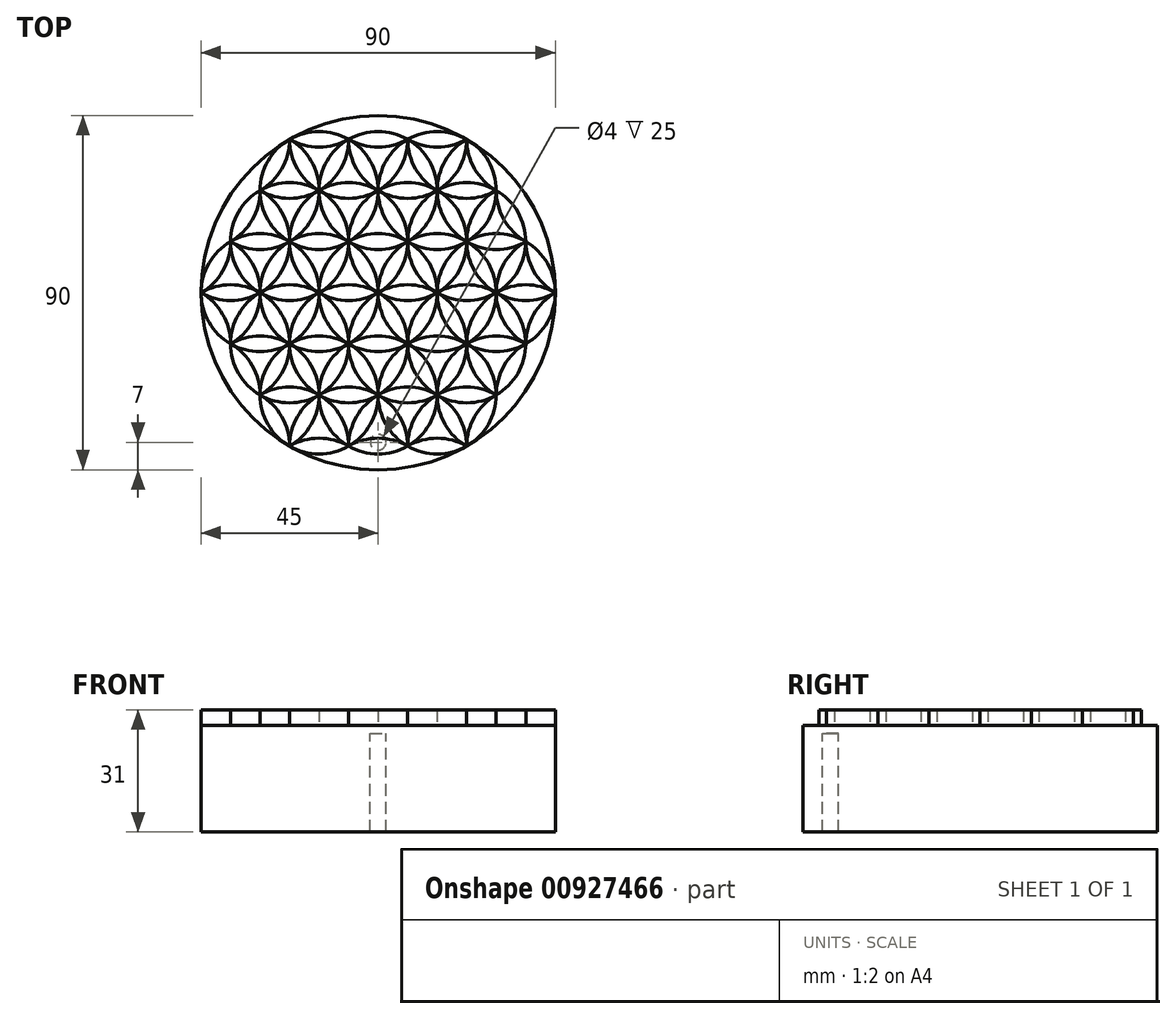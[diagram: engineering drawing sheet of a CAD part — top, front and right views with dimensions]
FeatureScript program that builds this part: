
annotation { "Feature Type Name" : "Feature", "Feature Type Description" : "" }
export const myFeature = defineFeature(function(context is Context, id is Id, definition is map)
    precondition{}
    {
        {
            var Q0;
            Q0=qCreatedBy(makeId("Top.planeOp"),FACE);
            var sketch = newSketch(context, id + "F0", { "sketchPlane" : qUnion([Q0])});
            skCircle(sketch, "E0", {"center": v(0, 0) * mm, "radius": 15 * mm});
            skCircle(sketch, "E1", {"center": v(15, 0) * mm, "radius": 15 * mm});
            skCircle(sketch, "E2", {"center": v(7.5, -13) * mm, "radius": 15 * mm});
            skCircle(sketch, "E3", {"center": v(-7.5, -13) * mm, "radius": 15 * mm});
            skCircle(sketch, "E4", {"center": v(-15, 0) * mm, "radius": 15 * mm});
            skCircle(sketch, "E5", {"center": v(-7.5, 13) * mm, "radius": 15 * mm});
            skCircle(sketch, "E6", {"center": v(7.5, 13) * mm, "radius": 15 * mm});
            skCircle(sketch, "E7", {"center": v(22.5, 13) * mm, "radius": 15 * mm});
            skCircle(sketch, "E8", {"center": v(-22.5, 13) * mm, "radius": 15 * mm});
            skCircle(sketch, "E9", {"center": v(-22.5, -13) * mm, "radius": 15 * mm});
            skCircle(sketch, "E10", {"center": v(-15, 25.98) * mm, "radius": 15 * mm});
            skCircle(sketch, "E11", {"center": v(0, 25.98) * mm, "radius": 15 * mm});
            skCircle(sketch, "E12", {"center": v(15, 25.98) * mm, "radius": 15 * mm});
            skCircle(sketch, "E13", {"center": v(7.5, 38.97) * mm, "radius": 15 * mm});
            skCircle(sketch, "E14", {"center": v(-7.5, 38.97) * mm, "radius": 15 * mm});
            skCircle(sketch, "E15", {"center": v(22.5, -13) * mm, "radius": 15 * mm});
            skCircle(sketch, "E16", {"center": v(30, 0) * mm, "radius": 15 * mm});
            skCircle(sketch, "E17", {"center": v(-30, 0) * mm, "radius": 15 * mm});
            skCircle(sketch, "E18", {"center": v(-15, -25.98) * mm, "radius": 15 * mm});
            skCircle(sketch, "E19", {"center": v(0, -25.98) * mm, "radius": 15 * mm});
            skCircle(sketch, "E20", {"center": v(15, -25.98) * mm, "radius": 15 * mm});
            skCircle(sketch, "E21", {"center": v(7.5, -38.97) * mm, "radius": 15 * mm});
            skCircle(sketch, "E22", {"center": v(-7.5, -38.97) * mm, "radius": 15 * mm});
            skCircle(sketch, "E23", {"center": v(30, -25.98) * mm, "radius": 15 * mm});
            skCircle(sketch, "E24", {"center": v(37.5, -13) * mm, "radius": 15 * mm});
            skCircle(sketch, "E25", {"center": v(-30, -25.98) * mm, "radius": 15 * mm});
            skCircle(sketch, "E26", {"center": v(-37.5, -13) * mm, "radius": 15 * mm});
            skCircle(sketch, "E27", {"center": v(-22.5, -38.97) * mm, "radius": 15 * mm});
            skCircle(sketch, "E28", {"center": v(22.5, -38.97) * mm, "radius": 15 * mm});
            skCircle(sketch, "E29", {"center": v(30, 25.98) * mm, "radius": 15 * mm});
            skCircle(sketch, "E30", {"center": v(37.5, 13) * mm, "radius": 15 * mm});
            skCircle(sketch, "E31", {"center": v(-30, 25.98) * mm, "radius": 15 * mm});
            skCircle(sketch, "E32", {"center": v(-37.5, 13) * mm, "radius": 15 * mm});
            skCircle(sketch, "E33", {"center": v(45, 0) * mm, "radius": 15 * mm});
            skCircle(sketch, "E34", {"center": v(45, -25.98) * mm, "radius": 15 * mm});
            skCircle(sketch, "E35", {"center": v(0, -51.96) * mm, "radius": 15 * mm});
            skCircle(sketch, "E36", {"center": v(0, 51.96) * mm, "radius": 15 * mm});
            skCircle(sketch, "E37", {"center": v(22.5, 38.97) * mm, "radius": 15 * mm});
            skCircle(sketch, "E38", {"center": v(-22.5, 38.97) * mm, "radius": 15 * mm});
            skCircle(sketch, "E39", {"center": v(-45, 0) * mm, "radius": 15 * mm});
            skCircle(sketch, "E40", {"center": v(-15, -51.96) * mm, "radius": 15 * mm});
            skCircle(sketch, "E41", {"center": v(15, -51.96) * mm, "radius": 15 * mm});
            skCircle(sketch, "E42", {"center": v(-45, -25.98) * mm, "radius": 15 * mm});
            skCircle(sketch, "E43", {"center": v(-37.5, -38.97) * mm, "radius": 15 * mm});
            skCircle(sketch, "E44", {"center": v(-52.5, 13) * mm, "radius": 15 * mm});
            skCircle(sketch, "E45", {"center": v(-45, 25.98) * mm, "radius": 15 * mm});
            skCircle(sketch, "E46", {"center": v(-37.5, 38.97) * mm, "radius": 15 * mm});
            skCircle(sketch, "E47", {"center": v(37.5, -38.97) * mm, "radius": 15 * mm});
            skCircle(sketch, "E48", {"center": v(-15, 51.96) * mm, "radius": 15 * mm});
            skCircle(sketch, "E49", {"center": v(-52.5, -13) * mm, "radius": 15 * mm});
            skCircle(sketch, "E50", {"center": v(15, 51.96) * mm, "radius": 15 * mm});
            skCircle(sketch, "E51", {"center": v(52.5, -13) * mm, "radius": 15 * mm});
            skCircle(sketch, "E52", {"center": v(37.5, 38.97) * mm, "radius": 15 * mm});
            skCircle(sketch, "E53", {"center": v(45, 25.98) * mm, "radius": 15 * mm});
            skCircle(sketch, "E54", {"center": v(52.5, 13) * mm, "radius": 15 * mm});
            skSolve(sketch);
        }
        {
            var Q0;
            {var subQ0=sQuery(id+"F0.wireOp",EDGE,"E6");var subQ1=sQuery(id+"F0.wireOp",EDGE,"E2");var subQ2=makeQuery(id+"F0.imprint","INTERSECT",VERTEX,{"derivedFrom":[sQuery(id+"F0.wireOp",EDGE,"E0"),subQ1,subQ0,sQuery(id+"F0.wireOp",EDGE,"E7"),sQuery(id+"F0.wireOp",EDGE,"E15"),sQuery(id+"F0.wireOp",EDGE,"E16")]});Q0=makeQuery(id+"F0.imprint","IMPRINT",FACE,{"disambiguationData":[TD([[makeQuery(id+"F0.imprint","IMPRINT",EDGE,{"disambiguationData":[TD([[subQ2,-1.0]])],"derivedFrom":subQ1}),1.0]])]});}
            var Q1;
            {var subQ0=sQuery(id+"F0.wireOp",EDGE,"E5");var subQ1=sQuery(id+"F0.wireOp",EDGE,"E1");var subQ2=makeQuery(id+"F0.imprint","INTERSECT",VERTEX,{"derivedFrom":[sQuery(id+"F0.wireOp",EDGE,"E0"),subQ1,subQ0,sQuery(id+"F0.wireOp",EDGE,"E7"),sQuery(id+"F0.wireOp",EDGE,"E11"),sQuery(id+"F0.wireOp",EDGE,"E12")]});Q1=makeQuery(id+"F0.imprint","IMPRINT",FACE,{"disambiguationData":[TD([[makeQuery(id+"F0.imprint","IMPRINT",EDGE,{"disambiguationData":[TD([[subQ2,-1.0]])],"derivedFrom":subQ1}),1.0]])]});}
            var Q2;
            {var subQ0=sQuery(id+"F0.wireOp",EDGE,"E6");var subQ1=sQuery(id+"F0.wireOp",EDGE,"E4");var subQ2=makeQuery(id+"F0.imprint","INTERSECT",VERTEX,{"derivedFrom":[sQuery(id+"F0.wireOp",EDGE,"E0"),subQ1,subQ0,sQuery(id+"F0.wireOp",EDGE,"E8"),sQuery(id+"F0.wireOp",EDGE,"E10"),sQuery(id+"F0.wireOp",EDGE,"E11")]});Q2=makeQuery(id+"F0.imprint","IMPRINT",FACE,{"disambiguationData":[TD([[makeQuery(id+"F0.imprint","IMPRINT",EDGE,{"disambiguationData":[TD([[subQ2,1.0]])],"derivedFrom":subQ1}),1.0]])]});}
            var Q3;
            {var subQ0=sQuery(id+"F0.wireOp",EDGE,"E5");var subQ1=sQuery(id+"F0.wireOp",EDGE,"E3");var subQ2=makeQuery(id+"F0.imprint","INTERSECT",VERTEX,{"derivedFrom":[sQuery(id+"F0.wireOp",EDGE,"E0"),subQ1,subQ0,sQuery(id+"F0.wireOp",EDGE,"E8"),sQuery(id+"F0.wireOp",EDGE,"E9"),sQuery(id+"F0.wireOp",EDGE,"E17")]});Q3=makeQuery(id+"F0.imprint","IMPRINT",FACE,{"disambiguationData":[TD([[makeQuery(id+"F0.imprint","IMPRINT",EDGE,{"disambiguationData":[TD([[subQ2,1.0]])],"derivedFrom":subQ1}),1.0]])]});}
            var Q4;
            {var subQ0=sQuery(id+"F0.wireOp",EDGE,"E4");var subQ1=sQuery(id+"F0.wireOp",EDGE,"E2");var subQ2=makeQuery(id+"F0.imprint","INTERSECT",VERTEX,{"derivedFrom":[sQuery(id+"F0.wireOp",EDGE,"E0"),subQ1,subQ0,sQuery(id+"F0.wireOp",EDGE,"E9"),sQuery(id+"F0.wireOp",EDGE,"E18"),sQuery(id+"F0.wireOp",EDGE,"E19")]});Q4=makeQuery(id+"F0.imprint","IMPRINT",FACE,{"disambiguationData":[TD([[makeQuery(id+"F0.imprint","IMPRINT",EDGE,{"disambiguationData":[TD([[subQ2,1.0]])],"derivedFrom":subQ1}),1.0]])]});}
            var Q5;
            {var subQ0=sQuery(id+"F0.wireOp",EDGE,"E3");var subQ1=sQuery(id+"F0.wireOp",EDGE,"E1");var subQ2=makeQuery(id+"F0.imprint","INTERSECT",VERTEX,{"derivedFrom":[sQuery(id+"F0.wireOp",EDGE,"E0"),subQ1,subQ0,sQuery(id+"F0.wireOp",EDGE,"E15"),sQuery(id+"F0.wireOp",EDGE,"E19"),sQuery(id+"F0.wireOp",EDGE,"E20")]});Q5=makeQuery(id+"F0.imprint","IMPRINT",FACE,{"disambiguationData":[TD([[makeQuery(id+"F0.imprint","IMPRINT",EDGE,{"disambiguationData":[TD([[subQ2,1.0]])],"derivedFrom":subQ1}),1.0]])]});}
            var Q6;
            {var subQ0=sQuery(id+"F0.wireOp",EDGE,"E15");var subQ1=sQuery(id+"F0.wireOp",EDGE,"E0");var subQ2=makeQuery(id+"F0.imprint","INTERSECT",VERTEX,{"derivedFrom":[subQ1,sQuery(id+"F0.wireOp",EDGE,"E2"),sQuery(id+"F0.wireOp",EDGE,"E6"),sQuery(id+"F0.wireOp",EDGE,"E7"),subQ0,sQuery(id+"F0.wireOp",EDGE,"E16")]});Q6=makeQuery(id+"F0.imprint","IMPRINT",FACE,{"disambiguationData":[TD([[makeQuery(id+"F0.imprint","IMPRINT",EDGE,{"disambiguationData":[TD([[subQ2,1.0]])],"derivedFrom":subQ1}),1.0]])]});}
            var Q7;
            {var subQ0=sQuery(id+"F0.wireOp",EDGE,"E7");var subQ1=sQuery(id+"F0.wireOp",EDGE,"E0");var subQ2=makeQuery(id+"F0.imprint","INTERSECT",VERTEX,{"derivedFrom":[subQ1,sQuery(id+"F0.wireOp",EDGE,"E1"),sQuery(id+"F0.wireOp",EDGE,"E5"),subQ0,sQuery(id+"F0.wireOp",EDGE,"E11"),sQuery(id+"F0.wireOp",EDGE,"E12")]});Q7=makeQuery(id+"F0.imprint","IMPRINT",FACE,{"disambiguationData":[TD([[makeQuery(id+"F0.imprint","IMPRINT",EDGE,{"disambiguationData":[TD([[subQ2,1.0]])],"derivedFrom":subQ1}),1.0]])]});}
            var Q8;
            {var subQ0=sQuery(id+"F0.wireOp",EDGE,"E11");var subQ1=sQuery(id+"F0.wireOp",EDGE,"E0");var subQ2=makeQuery(id+"F0.imprint","INTERSECT",VERTEX,{"derivedFrom":[subQ1,sQuery(id+"F0.wireOp",EDGE,"E1"),sQuery(id+"F0.wireOp",EDGE,"E5"),sQuery(id+"F0.wireOp",EDGE,"E7"),subQ0,sQuery(id+"F0.wireOp",EDGE,"E12")]});Q8=makeQuery(id+"F0.imprint","IMPRINT",FACE,{"disambiguationData":[TD([[makeQuery(id+"F0.imprint","IMPRINT",EDGE,{"disambiguationData":[TD([[subQ2,-1.0]])],"derivedFrom":subQ1}),1.0]])]});}
            var Q9;
            {var subQ0=sQuery(id+"F0.wireOp",EDGE,"E8");var subQ1=sQuery(id+"F0.wireOp",EDGE,"E0");var subQ2=makeQuery(id+"F0.imprint","INTERSECT",VERTEX,{"derivedFrom":[subQ1,sQuery(id+"F0.wireOp",EDGE,"E4"),sQuery(id+"F0.wireOp",EDGE,"E6"),subQ0,sQuery(id+"F0.wireOp",EDGE,"E10"),sQuery(id+"F0.wireOp",EDGE,"E11")]});Q9=makeQuery(id+"F0.imprint","IMPRINT",FACE,{"disambiguationData":[TD([[makeQuery(id+"F0.imprint","IMPRINT",EDGE,{"disambiguationData":[TD([[subQ2,-1.0]])],"derivedFrom":subQ1}),1.0]])]});}
            var Q10;
            {var subQ0=sQuery(id+"F0.wireOp",EDGE,"E9");var subQ1=sQuery(id+"F0.wireOp",EDGE,"E0");var subQ2=makeQuery(id+"F0.imprint","INTERSECT",VERTEX,{"derivedFrom":[subQ1,sQuery(id+"F0.wireOp",EDGE,"E3"),sQuery(id+"F0.wireOp",EDGE,"E5"),sQuery(id+"F0.wireOp",EDGE,"E8"),subQ0,sQuery(id+"F0.wireOp",EDGE,"E17")]});Q10=makeQuery(id+"F0.imprint","IMPRINT",FACE,{"disambiguationData":[TD([[makeQuery(id+"F0.imprint","IMPRINT",EDGE,{"disambiguationData":[TD([[subQ2,-1.0]])],"derivedFrom":subQ1}),1.0]])]});}
            var Q11;
            {var subQ0=sQuery(id+"F0.wireOp",EDGE,"E19");var subQ1=sQuery(id+"F0.wireOp",EDGE,"E0");var subQ2=makeQuery(id+"F0.imprint","INTERSECT",VERTEX,{"derivedFrom":[subQ1,sQuery(id+"F0.wireOp",EDGE,"E2"),sQuery(id+"F0.wireOp",EDGE,"E4"),sQuery(id+"F0.wireOp",EDGE,"E9"),sQuery(id+"F0.wireOp",EDGE,"E18"),subQ0]});Q11=makeQuery(id+"F0.imprint","IMPRINT",FACE,{"disambiguationData":[TD([[makeQuery(id+"F0.imprint","IMPRINT",EDGE,{"disambiguationData":[TD([[subQ2,-1.0]])],"derivedFrom":subQ1}),1.0]])]});}
            var Q12;
            {var subQ0=sQuery(id+"F0.wireOp",EDGE,"E18");var subQ1=sQuery(id+"F0.wireOp",EDGE,"E4");var subQ2=makeQuery(id+"F0.imprint","INTERSECT",VERTEX,{"derivedFrom":[sQuery(id+"F0.wireOp",EDGE,"E0"),sQuery(id+"F0.wireOp",EDGE,"E2"),subQ1,sQuery(id+"F0.wireOp",EDGE,"E9"),subQ0,sQuery(id+"F0.wireOp",EDGE,"E19")]});Q12=makeQuery(id+"F0.imprint","IMPRINT",FACE,{"disambiguationData":[TD([[makeQuery(id+"F0.imprint","IMPRINT",EDGE,{"disambiguationData":[TD([[subQ2,1.0]])],"derivedFrom":subQ1}),1.0]])]});}
            var Q13;
            {var subQ0=sQuery(id+"F0.wireOp",EDGE,"E19");var subQ1=sQuery(id+"F0.wireOp",EDGE,"E9");var subQ2=makeQuery(id+"F0.imprint","INTERSECT",VERTEX,{"derivedFrom":[sQuery(id+"F0.wireOp",EDGE,"E0"),sQuery(id+"F0.wireOp",EDGE,"E2"),sQuery(id+"F0.wireOp",EDGE,"E4"),subQ1,sQuery(id+"F0.wireOp",EDGE,"E18"),subQ0]});Q13=makeQuery(id+"F0.imprint","IMPRINT",FACE,{"disambiguationData":[TD([[makeQuery(id+"F0.imprint","IMPRINT",EDGE,{"disambiguationData":[TD([[subQ2,1.0]])],"derivedFrom":subQ1}),1.0]])]});}
            var Q14;
            {var subQ0=sQuery(id+"F0.wireOp",EDGE,"E18");var subQ1=sQuery(id+"F0.wireOp",EDGE,"E2");var subQ2=makeQuery(id+"F0.imprint","INTERSECT",VERTEX,{"derivedFrom":[sQuery(id+"F0.wireOp",EDGE,"E0"),subQ1,sQuery(id+"F0.wireOp",EDGE,"E4"),sQuery(id+"F0.wireOp",EDGE,"E9"),subQ0,sQuery(id+"F0.wireOp",EDGE,"E19")]});Q14=makeQuery(id+"F0.imprint","IMPRINT",FACE,{"disambiguationData":[TD([[makeQuery(id+"F0.imprint","IMPRINT",EDGE,{"disambiguationData":[TD([[subQ2,-1.0]])],"derivedFrom":subQ1}),1.0]])]});}
            var Q15;
            {var subQ0=sQuery(id+"F0.wireOp",EDGE,"E20");var subQ1=sQuery(id+"F0.wireOp",EDGE,"E3");var subQ2=makeQuery(id+"F0.imprint","INTERSECT",VERTEX,{"derivedFrom":[sQuery(id+"F0.wireOp",EDGE,"E0"),sQuery(id+"F0.wireOp",EDGE,"E1"),subQ1,sQuery(id+"F0.wireOp",EDGE,"E15"),sQuery(id+"F0.wireOp",EDGE,"E19"),subQ0]});Q15=makeQuery(id+"F0.imprint","IMPRINT",FACE,{"disambiguationData":[TD([[makeQuery(id+"F0.imprint","IMPRINT",EDGE,{"disambiguationData":[TD([[subQ2,1.0]])],"derivedFrom":subQ1}),1.0]])]});}
            var Q16;
            {var subQ0=sQuery(id+"F0.wireOp",EDGE,"E19");var subQ1=sQuery(id+"F0.wireOp",EDGE,"E15");var subQ2=makeQuery(id+"F0.imprint","INTERSECT",VERTEX,{"derivedFrom":[sQuery(id+"F0.wireOp",EDGE,"E0"),sQuery(id+"F0.wireOp",EDGE,"E1"),sQuery(id+"F0.wireOp",EDGE,"E3"),subQ1,subQ0,sQuery(id+"F0.wireOp",EDGE,"E20")]});Q16=makeQuery(id+"F0.imprint","IMPRINT",FACE,{"disambiguationData":[TD([[makeQuery(id+"F0.imprint","IMPRINT",EDGE,{"disambiguationData":[TD([[subQ2,-1.0]])],"derivedFrom":subQ1}),1.0]])]});}
            var Q17;
            {var subQ0=sQuery(id+"F0.wireOp",EDGE,"E20");var subQ1=sQuery(id+"F0.wireOp",EDGE,"E1");var subQ2=makeQuery(id+"F0.imprint","INTERSECT",VERTEX,{"derivedFrom":[sQuery(id+"F0.wireOp",EDGE,"E0"),subQ1,sQuery(id+"F0.wireOp",EDGE,"E3"),sQuery(id+"F0.wireOp",EDGE,"E15"),sQuery(id+"F0.wireOp",EDGE,"E19"),subQ0]});Q17=makeQuery(id+"F0.imprint","IMPRINT",FACE,{"disambiguationData":[TD([[makeQuery(id+"F0.imprint","IMPRINT",EDGE,{"disambiguationData":[TD([[subQ2,-1.0]])],"derivedFrom":subQ1}),1.0]])]});}
            var Q18;
            {var subQ0=sQuery(id+"F0.wireOp",EDGE,"E16");var subQ1=sQuery(id+"F0.wireOp",EDGE,"E2");var subQ2=makeQuery(id+"F0.imprint","INTERSECT",VERTEX,{"derivedFrom":[sQuery(id+"F0.wireOp",EDGE,"E0"),subQ1,sQuery(id+"F0.wireOp",EDGE,"E6"),sQuery(id+"F0.wireOp",EDGE,"E7"),sQuery(id+"F0.wireOp",EDGE,"E15"),subQ0]});Q18=makeQuery(id+"F0.imprint","IMPRINT",FACE,{"disambiguationData":[TD([[makeQuery(id+"F0.imprint","IMPRINT",EDGE,{"disambiguationData":[TD([[subQ2,1.0]])],"derivedFrom":subQ1}),1.0]])]});}
            var Q19;
            {var subQ0=sQuery(id+"F0.wireOp",EDGE,"E15");var subQ1=sQuery(id+"F0.wireOp",EDGE,"E7");var subQ2=makeQuery(id+"F0.imprint","INTERSECT",VERTEX,{"derivedFrom":[sQuery(id+"F0.wireOp",EDGE,"E0"),sQuery(id+"F0.wireOp",EDGE,"E2"),sQuery(id+"F0.wireOp",EDGE,"E6"),subQ1,subQ0,sQuery(id+"F0.wireOp",EDGE,"E16")]});Q19=makeQuery(id+"F0.imprint","IMPRINT",FACE,{"disambiguationData":[TD([[makeQuery(id+"F0.imprint","IMPRINT",EDGE,{"disambiguationData":[TD([[subQ2,-1.0]])],"derivedFrom":subQ1}),1.0]])]});}
            var Q20;
            {var subQ0=sQuery(id+"F0.wireOp",EDGE,"E16");var subQ1=sQuery(id+"F0.wireOp",EDGE,"E6");var subQ2=makeQuery(id+"F0.imprint","INTERSECT",VERTEX,{"derivedFrom":[sQuery(id+"F0.wireOp",EDGE,"E0"),sQuery(id+"F0.wireOp",EDGE,"E2"),subQ1,sQuery(id+"F0.wireOp",EDGE,"E7"),sQuery(id+"F0.wireOp",EDGE,"E15"),subQ0]});Q20=makeQuery(id+"F0.imprint","IMPRINT",FACE,{"disambiguationData":[TD([[makeQuery(id+"F0.imprint","IMPRINT",EDGE,{"disambiguationData":[TD([[subQ2,-1.0]])],"derivedFrom":subQ1}),1.0]])]});}
            var Q21;
            {var subQ0=sQuery(id+"F0.wireOp",EDGE,"E12");var subQ1=sQuery(id+"F0.wireOp",EDGE,"E1");var subQ2=makeQuery(id+"F0.imprint","INTERSECT",VERTEX,{"derivedFrom":[sQuery(id+"F0.wireOp",EDGE,"E0"),subQ1,sQuery(id+"F0.wireOp",EDGE,"E5"),sQuery(id+"F0.wireOp",EDGE,"E7"),sQuery(id+"F0.wireOp",EDGE,"E11"),subQ0]});Q21=makeQuery(id+"F0.imprint","IMPRINT",FACE,{"disambiguationData":[TD([[makeQuery(id+"F0.imprint","IMPRINT",EDGE,{"disambiguationData":[TD([[subQ2,1.0]])],"derivedFrom":subQ1}),1.0]])]});}
            var Q22;
            {var subQ0=sQuery(id+"F0.wireOp",EDGE,"E11");var subQ1=sQuery(id+"F0.wireOp",EDGE,"E7");var subQ2=makeQuery(id+"F0.imprint","INTERSECT",VERTEX,{"derivedFrom":[sQuery(id+"F0.wireOp",EDGE,"E0"),sQuery(id+"F0.wireOp",EDGE,"E1"),sQuery(id+"F0.wireOp",EDGE,"E5"),subQ1,subQ0,sQuery(id+"F0.wireOp",EDGE,"E12")]});Q22=makeQuery(id+"F0.imprint","IMPRINT",FACE,{"disambiguationData":[TD([[makeQuery(id+"F0.imprint","IMPRINT",EDGE,{"disambiguationData":[TD([[subQ2,1.0]])],"derivedFrom":subQ1}),1.0]])]});}
            var Q23;
            {var subQ0=sQuery(id+"F0.wireOp",EDGE,"E12");var subQ1=sQuery(id+"F0.wireOp",EDGE,"E5");var subQ2=makeQuery(id+"F0.imprint","INTERSECT",VERTEX,{"derivedFrom":[sQuery(id+"F0.wireOp",EDGE,"E0"),sQuery(id+"F0.wireOp",EDGE,"E1"),subQ1,sQuery(id+"F0.wireOp",EDGE,"E7"),sQuery(id+"F0.wireOp",EDGE,"E11"),subQ0]});Q23=makeQuery(id+"F0.imprint","IMPRINT",FACE,{"disambiguationData":[TD([[makeQuery(id+"F0.imprint","IMPRINT",EDGE,{"disambiguationData":[TD([[subQ2,-1.0]])],"derivedFrom":subQ1}),1.0]])]});}
            var Q24;
            {var subQ0=sQuery(id+"F0.wireOp",EDGE,"E10");var subQ1=sQuery(id+"F0.wireOp",EDGE,"E6");var subQ2=makeQuery(id+"F0.imprint","INTERSECT",VERTEX,{"derivedFrom":[sQuery(id+"F0.wireOp",EDGE,"E0"),sQuery(id+"F0.wireOp",EDGE,"E4"),subQ1,sQuery(id+"F0.wireOp",EDGE,"E8"),subQ0,sQuery(id+"F0.wireOp",EDGE,"E11")]});Q24=makeQuery(id+"F0.imprint","IMPRINT",FACE,{"disambiguationData":[TD([[makeQuery(id+"F0.imprint","IMPRINT",EDGE,{"disambiguationData":[TD([[subQ2,1.0]])],"derivedFrom":subQ1}),1.0]])]});}
            var Q25;
            {var subQ0=sQuery(id+"F0.wireOp",EDGE,"E11");var subQ1=sQuery(id+"F0.wireOp",EDGE,"E8");var subQ2=makeQuery(id+"F0.imprint","INTERSECT",VERTEX,{"derivedFrom":[sQuery(id+"F0.wireOp",EDGE,"E0"),sQuery(id+"F0.wireOp",EDGE,"E4"),sQuery(id+"F0.wireOp",EDGE,"E6"),subQ1,sQuery(id+"F0.wireOp",EDGE,"E10"),subQ0]});Q25=makeQuery(id+"F0.imprint","IMPRINT",FACE,{"disambiguationData":[TD([[makeQuery(id+"F0.imprint","IMPRINT",EDGE,{"disambiguationData":[TD([[subQ2,-1.0]])],"derivedFrom":subQ1}),1.0]])]});}
            var Q26;
            {var subQ0=sQuery(id+"F0.wireOp",EDGE,"E10");var subQ1=sQuery(id+"F0.wireOp",EDGE,"E4");var subQ2=makeQuery(id+"F0.imprint","INTERSECT",VERTEX,{"derivedFrom":[sQuery(id+"F0.wireOp",EDGE,"E0"),subQ1,sQuery(id+"F0.wireOp",EDGE,"E6"),sQuery(id+"F0.wireOp",EDGE,"E8"),subQ0,sQuery(id+"F0.wireOp",EDGE,"E11")]});Q26=makeQuery(id+"F0.imprint","IMPRINT",FACE,{"disambiguationData":[TD([[makeQuery(id+"F0.imprint","IMPRINT",EDGE,{"disambiguationData":[TD([[subQ2,-1.0]])],"derivedFrom":subQ1}),1.0]])]});}
            var Q27;
            {var subQ0=sQuery(id+"F0.wireOp",EDGE,"E17");var subQ1=sQuery(id+"F0.wireOp",EDGE,"E5");var subQ2=makeQuery(id+"F0.imprint","INTERSECT",VERTEX,{"derivedFrom":[sQuery(id+"F0.wireOp",EDGE,"E0"),sQuery(id+"F0.wireOp",EDGE,"E3"),subQ1,sQuery(id+"F0.wireOp",EDGE,"E8"),sQuery(id+"F0.wireOp",EDGE,"E9"),subQ0]});Q27=makeQuery(id+"F0.imprint","IMPRINT",FACE,{"disambiguationData":[TD([[makeQuery(id+"F0.imprint","IMPRINT",EDGE,{"disambiguationData":[TD([[subQ2,1.0]])],"derivedFrom":subQ1}),1.0]])]});}
            var Q28;
            {var subQ0=sQuery(id+"F0.wireOp",EDGE,"E9");var subQ1=sQuery(id+"F0.wireOp",EDGE,"E8");var subQ2=makeQuery(id+"F0.imprint","INTERSECT",VERTEX,{"derivedFrom":[sQuery(id+"F0.wireOp",EDGE,"E0"),sQuery(id+"F0.wireOp",EDGE,"E3"),sQuery(id+"F0.wireOp",EDGE,"E5"),subQ1,subQ0,sQuery(id+"F0.wireOp",EDGE,"E17")]});Q28=makeQuery(id+"F0.imprint","IMPRINT",FACE,{"disambiguationData":[TD([[makeQuery(id+"F0.imprint","IMPRINT",EDGE,{"disambiguationData":[TD([[subQ2,1.0]])],"derivedFrom":subQ1}),1.0]])]});}
            var Q29;
            {var subQ0=sQuery(id+"F0.wireOp",EDGE,"E17");var subQ1=sQuery(id+"F0.wireOp",EDGE,"E3");var subQ2=makeQuery(id+"F0.imprint","INTERSECT",VERTEX,{"derivedFrom":[sQuery(id+"F0.wireOp",EDGE,"E0"),subQ1,sQuery(id+"F0.wireOp",EDGE,"E5"),sQuery(id+"F0.wireOp",EDGE,"E8"),sQuery(id+"F0.wireOp",EDGE,"E9"),subQ0]});Q29=makeQuery(id+"F0.imprint","IMPRINT",FACE,{"disambiguationData":[TD([[makeQuery(id+"F0.imprint","IMPRINT",EDGE,{"disambiguationData":[TD([[subQ2,-1.0]])],"derivedFrom":subQ1}),1.0]])]});}
            var Q30;
            {var subQ0=sQuery(id+"F0.wireOp",EDGE,"E26");var subQ1=sQuery(id+"F0.wireOp",EDGE,"E4");var subQ2=makeQuery(id+"F0.imprint","INTERSECT",VERTEX,{"derivedFrom":[sQuery(id+"F0.wireOp",EDGE,"E3"),subQ1,sQuery(id+"F0.wireOp",EDGE,"E17"),sQuery(id+"F0.wireOp",EDGE,"E18"),sQuery(id+"F0.wireOp",EDGE,"E25"),subQ0]});Q30=makeQuery(id+"F0.imprint","IMPRINT",FACE,{"disambiguationData":[TD([[makeQuery(id+"F0.imprint","IMPRINT",EDGE,{"disambiguationData":[TD([[subQ2,1.0]])],"derivedFrom":subQ1}),1.0]])]});}
            var Q31;
            {var subQ0=sQuery(id+"F0.wireOp",EDGE,"E25");var subQ1=sQuery(id+"F0.wireOp",EDGE,"E3");var subQ2=makeQuery(id+"F0.imprint","INTERSECT",VERTEX,{"derivedFrom":[subQ1,sQuery(id+"F0.wireOp",EDGE,"E4"),sQuery(id+"F0.wireOp",EDGE,"E17"),sQuery(id+"F0.wireOp",EDGE,"E18"),subQ0,sQuery(id+"F0.wireOp",EDGE,"E26")]});Q31=makeQuery(id+"F0.imprint","IMPRINT",FACE,{"disambiguationData":[TD([[makeQuery(id+"F0.imprint","IMPRINT",EDGE,{"disambiguationData":[TD([[subQ2,-1.0]])],"derivedFrom":subQ1}),1.0]])]});}
            var Q32;
            {var subQ0=sQuery(id+"F0.wireOp",EDGE,"E22");var subQ1=sQuery(id+"F0.wireOp",EDGE,"E3");var subQ2=makeQuery(id+"F0.imprint","INTERSECT",VERTEX,{"derivedFrom":[sQuery(id+"F0.wireOp",EDGE,"E2"),subQ1,sQuery(id+"F0.wireOp",EDGE,"E18"),sQuery(id+"F0.wireOp",EDGE,"E20"),sQuery(id+"F0.wireOp",EDGE,"E21"),subQ0]});Q32=makeQuery(id+"F0.imprint","IMPRINT",FACE,{"disambiguationData":[TD([[makeQuery(id+"F0.imprint","IMPRINT",EDGE,{"disambiguationData":[TD([[subQ2,1.0]])],"derivedFrom":subQ1}),1.0]])]});}
            var Q33;
            {var subQ0=sQuery(id+"F0.wireOp",EDGE,"E21");var subQ1=sQuery(id+"F0.wireOp",EDGE,"E18");var subQ2=makeQuery(id+"F0.imprint","INTERSECT",VERTEX,{"derivedFrom":[sQuery(id+"F0.wireOp",EDGE,"E2"),sQuery(id+"F0.wireOp",EDGE,"E3"),subQ1,sQuery(id+"F0.wireOp",EDGE,"E20"),subQ0,sQuery(id+"F0.wireOp",EDGE,"E22")]});Q33=makeQuery(id+"F0.imprint","IMPRINT",FACE,{"disambiguationData":[TD([[makeQuery(id+"F0.imprint","IMPRINT",EDGE,{"disambiguationData":[TD([[subQ2,1.0]])],"derivedFrom":subQ1}),1.0]])]});}
            var Q34;
            {var subQ0=sQuery(id+"F0.wireOp",EDGE,"E21");var subQ1=sQuery(id+"F0.wireOp",EDGE,"E2");var subQ2=makeQuery(id+"F0.imprint","INTERSECT",VERTEX,{"derivedFrom":[subQ1,sQuery(id+"F0.wireOp",EDGE,"E3"),sQuery(id+"F0.wireOp",EDGE,"E18"),sQuery(id+"F0.wireOp",EDGE,"E20"),subQ0,sQuery(id+"F0.wireOp",EDGE,"E22")]});Q34=makeQuery(id+"F0.imprint","IMPRINT",FACE,{"disambiguationData":[TD([[makeQuery(id+"F0.imprint","IMPRINT",EDGE,{"disambiguationData":[TD([[subQ2,-1.0]])],"derivedFrom":subQ1}),1.0]])]});}
            var Q35;
            {var subQ0=sQuery(id+"F0.wireOp",EDGE,"E13");var subQ1=sQuery(id+"F0.wireOp",EDGE,"E6");var subQ2=makeQuery(id+"F0.imprint","INTERSECT",VERTEX,{"derivedFrom":[sQuery(id+"F0.wireOp",EDGE,"E5"),subQ1,sQuery(id+"F0.wireOp",EDGE,"E10"),sQuery(id+"F0.wireOp",EDGE,"E12"),subQ0,sQuery(id+"F0.wireOp",EDGE,"E14")]});Q35=makeQuery(id+"F0.imprint","IMPRINT",FACE,{"disambiguationData":[TD([[makeQuery(id+"F0.imprint","IMPRINT",EDGE,{"disambiguationData":[TD([[subQ2,1.0]])],"derivedFrom":subQ1}),1.0]])]});}
            var Q36;
            {var subQ0=sQuery(id+"F0.wireOp",EDGE,"E14");var subQ1=sQuery(id+"F0.wireOp",EDGE,"E12");var subQ2=makeQuery(id+"F0.imprint","INTERSECT",VERTEX,{"derivedFrom":[sQuery(id+"F0.wireOp",EDGE,"E11"),subQ1,subQ0,sQuery(id+"F0.wireOp",EDGE,"E36"),sQuery(id+"F0.wireOp",EDGE,"E37")]});Q36=makeQuery(id+"F0.imprint","IMPRINT",FACE,{"disambiguationData":[TD([[makeQuery(id+"F0.imprint","IMPRINT",EDGE,{"disambiguationData":[TD([[subQ2,-1.0]])],"derivedFrom":subQ1}),1.0]])]});}
            var Q37;
            {var subQ0=sQuery(id+"F0.wireOp",EDGE,"E13");var subQ1=sQuery(id+"F0.wireOp",EDGE,"E10");var subQ2=makeQuery(id+"F0.imprint","INTERSECT",VERTEX,{"derivedFrom":[subQ1,sQuery(id+"F0.wireOp",EDGE,"E11"),subQ0,sQuery(id+"F0.wireOp",EDGE,"E36"),sQuery(id+"F0.wireOp",EDGE,"E38")]});Q37=makeQuery(id+"F0.imprint","IMPRINT",FACE,{"disambiguationData":[TD([[makeQuery(id+"F0.imprint","IMPRINT",EDGE,{"disambiguationData":[TD([[subQ2,1.0]])],"derivedFrom":subQ1}),1.0]])]});}
            var Q38;
            {var subQ0=sQuery(id+"F0.wireOp",EDGE,"E14");var subQ1=sQuery(id+"F0.wireOp",EDGE,"E5");var subQ2=makeQuery(id+"F0.imprint","INTERSECT",VERTEX,{"derivedFrom":[subQ1,sQuery(id+"F0.wireOp",EDGE,"E6"),sQuery(id+"F0.wireOp",EDGE,"E10"),sQuery(id+"F0.wireOp",EDGE,"E12"),sQuery(id+"F0.wireOp",EDGE,"E13"),subQ0]});Q38=makeQuery(id+"F0.imprint","IMPRINT",FACE,{"disambiguationData":[TD([[makeQuery(id+"F0.imprint","IMPRINT",EDGE,{"disambiguationData":[TD([[subQ2,-1.0]])],"derivedFrom":subQ1}),1.0]])]});}
            var Q39;
            {var subQ0=sQuery(id+"F0.wireOp",EDGE,"E36");var subQ1=sQuery(id+"F0.wireOp",EDGE,"E11");var subQ2=makeQuery(id+"F0.imprint","INTERSECT",VERTEX,{"derivedFrom":[sQuery(id+"F0.wireOp",EDGE,"E10"),subQ1,sQuery(id+"F0.wireOp",EDGE,"E13"),subQ0,sQuery(id+"F0.wireOp",EDGE,"E38")]});Q39=makeQuery(id+"F0.imprint","IMPRINT",FACE,{"disambiguationData":[TD([[makeQuery(id+"F0.imprint","IMPRINT",EDGE,{"disambiguationData":[TD([[subQ2,1.0]])],"derivedFrom":subQ1}),1.0]])]});}
            var Q40;
            {var subQ0=sQuery(id+"F0.wireOp",EDGE,"E37");var subQ1=sQuery(id+"F0.wireOp",EDGE,"E11");var subQ2=makeQuery(id+"F0.imprint","INTERSECT",VERTEX,{"derivedFrom":[subQ1,sQuery(id+"F0.wireOp",EDGE,"E12"),sQuery(id+"F0.wireOp",EDGE,"E14"),sQuery(id+"F0.wireOp",EDGE,"E36"),subQ0]});Q40=makeQuery(id+"F0.imprint","IMPRINT",FACE,{"disambiguationData":[TD([[makeQuery(id+"F0.imprint","IMPRINT",EDGE,{"disambiguationData":[TD([[subQ2,1.0]])],"derivedFrom":subQ1}),1.0]])]});}
            var Q41;
            {var subQ0=sQuery(id+"F0.wireOp",EDGE,"E29");var subQ1=sQuery(id+"F0.wireOp",EDGE,"E6");var subQ2=makeQuery(id+"F0.imprint","INTERSECT",VERTEX,{"derivedFrom":[sQuery(id+"F0.wireOp",EDGE,"E1"),subQ1,sQuery(id+"F0.wireOp",EDGE,"E12"),sQuery(id+"F0.wireOp",EDGE,"E16"),subQ0,sQuery(id+"F0.wireOp",EDGE,"E30")]});Q41=makeQuery(id+"F0.imprint","IMPRINT",FACE,{"disambiguationData":[TD([[makeQuery(id+"F0.imprint","IMPRINT",EDGE,{"disambiguationData":[TD([[subQ2,-1.0]])],"derivedFrom":subQ1}),1.0]])]});}
            var Q42;
            {var subQ0=sQuery(id+"F0.wireOp",EDGE,"E30");var subQ1=sQuery(id+"F0.wireOp",EDGE,"E1");var subQ2=makeQuery(id+"F0.imprint","INTERSECT",VERTEX,{"derivedFrom":[subQ1,sQuery(id+"F0.wireOp",EDGE,"E6"),sQuery(id+"F0.wireOp",EDGE,"E12"),sQuery(id+"F0.wireOp",EDGE,"E16"),sQuery(id+"F0.wireOp",EDGE,"E29"),subQ0]});Q42=makeQuery(id+"F0.imprint","IMPRINT",FACE,{"disambiguationData":[TD([[makeQuery(id+"F0.imprint","IMPRINT",EDGE,{"disambiguationData":[TD([[subQ2,1.0]])],"derivedFrom":subQ1}),1.0]])]});}
            var Q43;
            {var subQ0=sQuery(id+"F0.wireOp",EDGE,"E24");var subQ1=sQuery(id+"F0.wireOp",EDGE,"E1");var subQ2=makeQuery(id+"F0.imprint","INTERSECT",VERTEX,{"derivedFrom":[subQ1,sQuery(id+"F0.wireOp",EDGE,"E7"),sQuery(id+"F0.wireOp",EDGE,"E15"),subQ0,sQuery(id+"F0.wireOp",EDGE,"E30"),sQuery(id+"F0.wireOp",EDGE,"E33")]});Q43=makeQuery(id+"F0.imprint","IMPRINT",FACE,{"disambiguationData":[TD([[makeQuery(id+"F0.imprint","IMPRINT",EDGE,{"disambiguationData":[TD([[subQ2,1.0]])],"derivedFrom":subQ1}),1.0]])]});}
            var Q44;
            {var subQ0=sQuery(id+"F0.wireOp",EDGE,"E23");var subQ1=sQuery(id+"F0.wireOp",EDGE,"E2");var subQ2=makeQuery(id+"F0.imprint","INTERSECT",VERTEX,{"derivedFrom":[sQuery(id+"F0.wireOp",EDGE,"E1"),subQ1,sQuery(id+"F0.wireOp",EDGE,"E16"),sQuery(id+"F0.wireOp",EDGE,"E20"),subQ0,sQuery(id+"F0.wireOp",EDGE,"E24")]});Q44=makeQuery(id+"F0.imprint","IMPRINT",FACE,{"disambiguationData":[TD([[makeQuery(id+"F0.imprint","IMPRINT",EDGE,{"disambiguationData":[TD([[subQ2,1.0]])],"derivedFrom":subQ1}),1.0]])]});}
            var Q45;
            {var subQ0=sQuery(id+"F0.wireOp",EDGE,"E28");var subQ1=sQuery(id+"F0.wireOp",EDGE,"E19");var subQ2=makeQuery(id+"F0.imprint","INTERSECT",VERTEX,{"derivedFrom":[sQuery(id+"F0.wireOp",EDGE,"E2"),sQuery(id+"F0.wireOp",EDGE,"E15"),subQ1,sQuery(id+"F0.wireOp",EDGE,"E21"),sQuery(id+"F0.wireOp",EDGE,"E23"),subQ0]});Q45=makeQuery(id+"F0.imprint","IMPRINT",FACE,{"disambiguationData":[TD([[makeQuery(id+"F0.imprint","IMPRINT",EDGE,{"disambiguationData":[TD([[subQ2,1.0]])],"derivedFrom":subQ1}),1.0]])]});}
            var Q46;
            {var subQ0=sQuery(id+"F0.wireOp",EDGE,"E22");var subQ1=sQuery(id+"F0.wireOp",EDGE,"E20");var subQ2=makeQuery(id+"F0.imprint","INTERSECT",VERTEX,{"derivedFrom":[sQuery(id+"F0.wireOp",EDGE,"E2"),sQuery(id+"F0.wireOp",EDGE,"E3"),sQuery(id+"F0.wireOp",EDGE,"E18"),subQ1,sQuery(id+"F0.wireOp",EDGE,"E21"),subQ0]});Q46=makeQuery(id+"F0.imprint","IMPRINT",FACE,{"disambiguationData":[TD([[makeQuery(id+"F0.imprint","IMPRINT",EDGE,{"disambiguationData":[TD([[subQ2,-1.0]])],"derivedFrom":subQ1}),1.0]])]});}
            var Q47;
            {var subQ0=sQuery(id+"F0.wireOp",EDGE,"E35");var subQ1=sQuery(id+"F0.wireOp",EDGE,"E19");var subQ2=makeQuery(id+"F0.imprint","INTERSECT",VERTEX,{"derivedFrom":[sQuery(id+"F0.wireOp",EDGE,"E18"),subQ1,sQuery(id+"F0.wireOp",EDGE,"E21"),sQuery(id+"F0.wireOp",EDGE,"E27"),subQ0,sQuery(id+"F0.wireOp",EDGE,"E40")]});Q47=makeQuery(id+"F0.imprint","IMPRINT",FACE,{"disambiguationData":[TD([[makeQuery(id+"F0.imprint","IMPRINT",EDGE,{"disambiguationData":[TD([[subQ2,-1.0]])],"derivedFrom":subQ1}),1.0]])]});}
            var Q48;
            {var subQ0=sQuery(id+"F0.wireOp",EDGE,"E27");var subQ1=sQuery(id+"F0.wireOp",EDGE,"E19");var subQ2=makeQuery(id+"F0.imprint","INTERSECT",VERTEX,{"derivedFrom":[sQuery(id+"F0.wireOp",EDGE,"E3"),sQuery(id+"F0.wireOp",EDGE,"E9"),subQ1,sQuery(id+"F0.wireOp",EDGE,"E22"),sQuery(id+"F0.wireOp",EDGE,"E25"),subQ0]});Q48=makeQuery(id+"F0.imprint","IMPRINT",FACE,{"disambiguationData":[TD([[makeQuery(id+"F0.imprint","IMPRINT",EDGE,{"disambiguationData":[TD([[subQ2,-1.0]])],"derivedFrom":subQ1}),1.0]])]});}
            var Q49;
            {var subQ0=sQuery(id+"F0.wireOp",EDGE,"E32");var subQ1=sQuery(id+"F0.wireOp",EDGE,"E4");var subQ2=makeQuery(id+"F0.imprint","INTERSECT",VERTEX,{"derivedFrom":[subQ1,sQuery(id+"F0.wireOp",EDGE,"E5"),sQuery(id+"F0.wireOp",EDGE,"E10"),sQuery(id+"F0.wireOp",EDGE,"E17"),sQuery(id+"F0.wireOp",EDGE,"E31"),subQ0]});Q49=makeQuery(id+"F0.imprint","IMPRINT",FACE,{"disambiguationData":[TD([[makeQuery(id+"F0.imprint","IMPRINT",EDGE,{"disambiguationData":[TD([[subQ2,-1.0]])],"derivedFrom":subQ1}),1.0]])]});}
            var Q50;
            {var subQ0=sQuery(id+"F0.wireOp",EDGE,"E31");var subQ1=sQuery(id+"F0.wireOp",EDGE,"E5");var subQ2=makeQuery(id+"F0.imprint","INTERSECT",VERTEX,{"derivedFrom":[sQuery(id+"F0.wireOp",EDGE,"E4"),subQ1,sQuery(id+"F0.wireOp",EDGE,"E10"),sQuery(id+"F0.wireOp",EDGE,"E17"),subQ0,sQuery(id+"F0.wireOp",EDGE,"E32")]});Q50=makeQuery(id+"F0.imprint","IMPRINT",FACE,{"disambiguationData":[TD([[makeQuery(id+"F0.imprint","IMPRINT",EDGE,{"disambiguationData":[TD([[subQ2,1.0]])],"derivedFrom":subQ1}),1.0]])]});}
            var Q51;
            {var subQ0=sQuery(id+"F0.wireOp",EDGE,"E38");var subQ1=sQuery(id+"F0.wireOp",EDGE,"E11");var subQ2=makeQuery(id+"F0.imprint","INTERSECT",VERTEX,{"derivedFrom":[sQuery(id+"F0.wireOp",EDGE,"E10"),subQ1,sQuery(id+"F0.wireOp",EDGE,"E13"),sQuery(id+"F0.wireOp",EDGE,"E36"),subQ0]});Q51=makeQuery(id+"F0.imprint","IMPRINT",FACE,{"disambiguationData":[TD([[makeQuery(id+"F0.imprint","IMPRINT",EDGE,{"disambiguationData":[TD([[subQ2,-1.0]])],"derivedFrom":subQ1}),1.0]])]});}
            var Q52;
            {var subQ0=sQuery(id+"F0.wireOp",EDGE,"E41");var subQ1=sQuery(id+"F0.wireOp",EDGE,"E20");var subQ2=makeQuery(id+"F0.imprint","INTERSECT",VERTEX,{"derivedFrom":[sQuery(id+"F0.wireOp",EDGE,"E19"),subQ1,sQuery(id+"F0.wireOp",EDGE,"E22"),sQuery(id+"F0.wireOp",EDGE,"E28"),sQuery(id+"F0.wireOp",EDGE,"E35"),subQ0]});Q52=makeQuery(id+"F0.imprint","IMPRINT",FACE,{"disambiguationData":[TD([[makeQuery(id+"F0.imprint","IMPRINT",EDGE,{"disambiguationData":[TD([[subQ2,-1.0]])],"derivedFrom":subQ1}),1.0]])]});}
            var Q53;
            {var subQ0=sQuery(id+"F0.wireOp",EDGE,"E23");var subQ1=sQuery(id+"F0.wireOp",EDGE,"E21");var subQ2=makeQuery(id+"F0.imprint","INTERSECT",VERTEX,{"derivedFrom":[sQuery(id+"F0.wireOp",EDGE,"E2"),sQuery(id+"F0.wireOp",EDGE,"E15"),sQuery(id+"F0.wireOp",EDGE,"E19"),subQ1,subQ0,sQuery(id+"F0.wireOp",EDGE,"E28")]});Q53=makeQuery(id+"F0.imprint","IMPRINT",FACE,{"disambiguationData":[TD([[makeQuery(id+"F0.imprint","IMPRINT",EDGE,{"disambiguationData":[TD([[subQ2,1.0]])],"derivedFrom":subQ1}),1.0]])]});}
            var Q54;
            {var subQ0=sQuery(id+"F0.wireOp",EDGE,"E47");var subQ1=sQuery(id+"F0.wireOp",EDGE,"E20");var subQ2=makeQuery(id+"F0.imprint","INTERSECT",VERTEX,{"derivedFrom":[sQuery(id+"F0.wireOp",EDGE,"E15"),subQ1,sQuery(id+"F0.wireOp",EDGE,"E24"),sQuery(id+"F0.wireOp",EDGE,"E28"),sQuery(id+"F0.wireOp",EDGE,"E34"),subQ0]});Q54=makeQuery(id+"F0.imprint","IMPRINT",FACE,{"disambiguationData":[TD([[makeQuery(id+"F0.imprint","IMPRINT",EDGE,{"disambiguationData":[TD([[subQ2,1.0]])],"derivedFrom":subQ1}),1.0]])]});}
            var Q55;
            {var subQ0=sQuery(id+"F0.wireOp",EDGE,"E28");var subQ1=sQuery(id+"F0.wireOp",EDGE,"E15");var subQ2=makeQuery(id+"F0.imprint","INTERSECT",VERTEX,{"derivedFrom":[sQuery(id+"F0.wireOp",EDGE,"E2"),subQ1,sQuery(id+"F0.wireOp",EDGE,"E19"),sQuery(id+"F0.wireOp",EDGE,"E21"),sQuery(id+"F0.wireOp",EDGE,"E23"),subQ0]});Q55=makeQuery(id+"F0.imprint","IMPRINT",FACE,{"disambiguationData":[TD([[makeQuery(id+"F0.imprint","IMPRINT",EDGE,{"disambiguationData":[TD([[subQ2,-1.0]])],"derivedFrom":subQ1}),1.0]])]});}
            var Q56;
            {var subQ0=sQuery(id+"F0.wireOp",EDGE,"E24");var subQ1=sQuery(id+"F0.wireOp",EDGE,"E20");var subQ2=makeQuery(id+"F0.imprint","INTERSECT",VERTEX,{"derivedFrom":[sQuery(id+"F0.wireOp",EDGE,"E1"),sQuery(id+"F0.wireOp",EDGE,"E2"),sQuery(id+"F0.wireOp",EDGE,"E16"),subQ1,sQuery(id+"F0.wireOp",EDGE,"E23"),subQ0]});Q56=makeQuery(id+"F0.imprint","IMPRINT",FACE,{"disambiguationData":[TD([[makeQuery(id+"F0.imprint","IMPRINT",EDGE,{"disambiguationData":[TD([[subQ2,1.0]])],"derivedFrom":subQ1}),1.0]])]});}
            var Q57;
            {var subQ0=sQuery(id+"F0.wireOp",EDGE,"E34");var subQ1=sQuery(id+"F0.wireOp",EDGE,"E15");var subQ2=makeQuery(id+"F0.imprint","INTERSECT",VERTEX,{"derivedFrom":[subQ1,sQuery(id+"F0.wireOp",EDGE,"E16"),sQuery(id+"F0.wireOp",EDGE,"E23"),sQuery(id+"F0.wireOp",EDGE,"E33"),subQ0]});Q57=makeQuery(id+"F0.imprint","IMPRINT",FACE,{"disambiguationData":[TD([[makeQuery(id+"F0.imprint","IMPRINT",EDGE,{"disambiguationData":[TD([[subQ2,1.0]])],"derivedFrom":subQ1}),1.0]])]});}
            var Q58;
            {var subQ0=sQuery(id+"F0.wireOp",EDGE,"E23");var subQ1=sQuery(id+"F0.wireOp",EDGE,"E16");var subQ2=makeQuery(id+"F0.imprint","INTERSECT",VERTEX,{"derivedFrom":[sQuery(id+"F0.wireOp",EDGE,"E15"),subQ1,subQ0,sQuery(id+"F0.wireOp",EDGE,"E33"),sQuery(id+"F0.wireOp",EDGE,"E34")]});Q58=makeQuery(id+"F0.imprint","IMPRINT",FACE,{"disambiguationData":[TD([[makeQuery(id+"F0.imprint","IMPRINT",EDGE,{"disambiguationData":[TD([[subQ2,1.0]])],"derivedFrom":subQ1}),1.0]])]});}
            var Q59;
            {var subQ0=sQuery(id+"F0.wireOp",EDGE,"E33");var subQ1=sQuery(id+"F0.wireOp",EDGE,"E15");var subQ2=makeQuery(id+"F0.imprint","INTERSECT",VERTEX,{"derivedFrom":[subQ1,sQuery(id+"F0.wireOp",EDGE,"E16"),sQuery(id+"F0.wireOp",EDGE,"E23"),subQ0,sQuery(id+"F0.wireOp",EDGE,"E34")]});Q59=makeQuery(id+"F0.imprint","IMPRINT",FACE,{"disambiguationData":[TD([[makeQuery(id+"F0.imprint","IMPRINT",EDGE,{"disambiguationData":[TD([[subQ2,-1.0]])],"derivedFrom":subQ1}),1.0]])]});}
            var Q60;
            {var subQ0=sQuery(id+"F0.wireOp",EDGE,"E40");var subQ1=sQuery(id+"F0.wireOp",EDGE,"E18");var subQ2=makeQuery(id+"F0.imprint","INTERSECT",VERTEX,{"derivedFrom":[subQ1,sQuery(id+"F0.wireOp",EDGE,"E22"),sQuery(id+"F0.wireOp",EDGE,"E25"),subQ0,sQuery(id+"F0.wireOp",EDGE,"4keGgqQS-VjFO-Uu6F-eGOx-LwLd6920sbIl"),sQuery(id+"F0.wireOp",EDGE,"E43")]});Q60=makeQuery(id+"F0.imprint","IMPRINT",FACE,{"disambiguationData":[TD([[makeQuery(id+"F0.imprint","IMPRINT",EDGE,{"disambiguationData":[TD([[subQ2,-1.0]])],"derivedFrom":subQ1}),1.0]])]});}
            var Q61;
            {var subQ0=sQuery(id+"F0.wireOp",EDGE,"E25");var subQ1=sQuery(id+"F0.wireOp",EDGE,"E22");var subQ2=makeQuery(id+"F0.imprint","INTERSECT",VERTEX,{"derivedFrom":[sQuery(id+"F0.wireOp",EDGE,"E3"),sQuery(id+"F0.wireOp",EDGE,"E9"),sQuery(id+"F0.wireOp",EDGE,"E19"),subQ1,subQ0,sQuery(id+"F0.wireOp",EDGE,"E27")]});Q61=makeQuery(id+"F0.imprint","IMPRINT",FACE,{"disambiguationData":[TD([[makeQuery(id+"F0.imprint","IMPRINT",EDGE,{"disambiguationData":[TD([[subQ2,-1.0]])],"derivedFrom":subQ1}),1.0]])]});}
            var Q62;
            {var subQ0=sQuery(id+"F0.wireOp",EDGE,"E27");var subQ1=sQuery(id+"F0.wireOp",EDGE,"E9");var subQ2=makeQuery(id+"F0.imprint","INTERSECT",VERTEX,{"derivedFrom":[sQuery(id+"F0.wireOp",EDGE,"E3"),subQ1,sQuery(id+"F0.wireOp",EDGE,"E19"),sQuery(id+"F0.wireOp",EDGE,"E22"),sQuery(id+"F0.wireOp",EDGE,"E25"),subQ0]});Q62=makeQuery(id+"F0.imprint","IMPRINT",FACE,{"disambiguationData":[TD([[makeQuery(id+"F0.imprint","IMPRINT",EDGE,{"disambiguationData":[TD([[subQ2,1.0]])],"derivedFrom":subQ1}),1.0]])]});}
            var Q63;
            {var subQ0=sQuery(id+"F0.wireOp",EDGE,"E43");var subQ1=sQuery(id+"F0.wireOp",EDGE,"E18");var subQ2=makeQuery(id+"F0.imprint","INTERSECT",VERTEX,{"derivedFrom":[sQuery(id+"F0.wireOp",EDGE,"E9"),subQ1,sQuery(id+"F0.wireOp",EDGE,"E26"),sQuery(id+"F0.wireOp",EDGE,"E27"),sQuery(id+"F0.wireOp",EDGE,"E42"),subQ0]});Q63=makeQuery(id+"F0.imprint","IMPRINT",FACE,{"disambiguationData":[TD([[makeQuery(id+"F0.imprint","IMPRINT",EDGE,{"disambiguationData":[TD([[subQ2,-1.0]])],"derivedFrom":subQ1}),1.0]])]});}
            var Q64;
            {var subQ0=sQuery(id+"F0.wireOp",EDGE,"E26");var subQ1=sQuery(id+"F0.wireOp",EDGE,"E18");var subQ2=makeQuery(id+"F0.imprint","INTERSECT",VERTEX,{"derivedFrom":[sQuery(id+"F0.wireOp",EDGE,"E3"),sQuery(id+"F0.wireOp",EDGE,"E4"),sQuery(id+"F0.wireOp",EDGE,"E17"),subQ1,sQuery(id+"F0.wireOp",EDGE,"E25"),subQ0]});Q64=makeQuery(id+"F0.imprint","IMPRINT",FACE,{"disambiguationData":[TD([[makeQuery(id+"F0.imprint","IMPRINT",EDGE,{"disambiguationData":[TD([[subQ2,-1.0]])],"derivedFrom":subQ1}),1.0]])]});}
            var Q65;
            {var subQ0=sQuery(id+"F0.wireOp",EDGE,"E42");var subQ1=sQuery(id+"F0.wireOp",EDGE,"E9");var subQ2=makeQuery(id+"F0.imprint","INTERSECT",VERTEX,{"derivedFrom":[subQ1,sQuery(id+"F0.wireOp",EDGE,"E17"),sQuery(id+"F0.wireOp",EDGE,"E25"),sQuery(id+"F0.wireOp",EDGE,"E39"),subQ0]});Q65=makeQuery(id+"F0.imprint","IMPRINT",FACE,{"disambiguationData":[TD([[makeQuery(id+"F0.imprint","IMPRINT",EDGE,{"disambiguationData":[TD([[subQ2,-1.0]])],"derivedFrom":subQ1}),1.0]])]});}
            var Q66;
            {var subQ0=sQuery(id+"F0.wireOp",EDGE,"E25");var subQ1=sQuery(id+"F0.wireOp",EDGE,"E17");var subQ2=makeQuery(id+"F0.imprint","INTERSECT",VERTEX,{"derivedFrom":[sQuery(id+"F0.wireOp",EDGE,"E9"),subQ1,subQ0,sQuery(id+"F0.wireOp",EDGE,"E39"),sQuery(id+"F0.wireOp",EDGE,"E42")]});Q66=makeQuery(id+"F0.imprint","IMPRINT",FACE,{"disambiguationData":[TD([[makeQuery(id+"F0.imprint","IMPRINT",EDGE,{"disambiguationData":[TD([[subQ2,-1.0]])],"derivedFrom":subQ1}),1.0]])]});}
            var Q67;
            {var subQ0=sQuery(id+"F0.wireOp",EDGE,"E39");var subQ1=sQuery(id+"F0.wireOp",EDGE,"E9");var subQ2=makeQuery(id+"F0.imprint","INTERSECT",VERTEX,{"derivedFrom":[subQ1,sQuery(id+"F0.wireOp",EDGE,"E17"),sQuery(id+"F0.wireOp",EDGE,"E25"),subQ0,sQuery(id+"F0.wireOp",EDGE,"E42")]});Q67=makeQuery(id+"F0.imprint","IMPRINT",FACE,{"disambiguationData":[TD([[makeQuery(id+"F0.imprint","IMPRINT",EDGE,{"disambiguationData":[TD([[subQ2,1.0]])],"derivedFrom":subQ1}),1.0]])]});}
            var Q68;
            {var subQ0=sQuery(id+"F0.wireOp",EDGE,"E49");var subQ1=sQuery(id+"F0.wireOp",EDGE,"E17");var subQ2=makeQuery(id+"F0.imprint","INTERSECT",VERTEX,{"derivedFrom":[subQ1,sQuery(id+"F0.wireOp",EDGE,"E26"),sQuery(id+"F0.wireOp",EDGE,"E32"),sQuery(id+"F0.wireOp",EDGE,"E44"),subQ0]});Q68=makeQuery(id+"F0.imprint","IMPRINT",FACE,{"disambiguationData":[TD([[makeQuery(id+"F0.imprint","IMPRINT",EDGE,{"disambiguationData":[TD([[subQ2,-1.0]])],"derivedFrom":subQ1}),1.0]])]});}
            var Q69;
            {var subQ0=sQuery(id+"F0.wireOp",EDGE,"E32");var subQ1=sQuery(id+"F0.wireOp",EDGE,"E26");var subQ2=makeQuery(id+"F0.imprint","INTERSECT",VERTEX,{"derivedFrom":[sQuery(id+"F0.wireOp",EDGE,"E17"),subQ1,subQ0,sQuery(id+"F0.wireOp",EDGE,"E44"),sQuery(id+"F0.wireOp",EDGE,"E49")]});Q69=makeQuery(id+"F0.imprint","IMPRINT",FACE,{"disambiguationData":[TD([[makeQuery(id+"F0.imprint","IMPRINT",EDGE,{"disambiguationData":[TD([[subQ2,1.0]])],"derivedFrom":subQ1}),1.0]])]});}
            var Q70;
            {var subQ0=sQuery(id+"F0.wireOp",EDGE,"E44");var subQ1=sQuery(id+"F0.wireOp",EDGE,"E17");var subQ2=makeQuery(id+"F0.imprint","INTERSECT",VERTEX,{"derivedFrom":[subQ1,sQuery(id+"F0.wireOp",EDGE,"E26"),sQuery(id+"F0.wireOp",EDGE,"E32"),subQ0,sQuery(id+"F0.wireOp",EDGE,"E49")]});Q70=makeQuery(id+"F0.imprint","IMPRINT",FACE,{"disambiguationData":[TD([[makeQuery(id+"F0.imprint","IMPRINT",EDGE,{"disambiguationData":[TD([[subQ2,1.0]])],"derivedFrom":subQ1}),1.0]])]});}
            var Q71;
            {var subQ0=sQuery(id+"F0.wireOp",EDGE,"E39");var subQ1=sQuery(id+"F0.wireOp",EDGE,"E8");var subQ2=makeQuery(id+"F0.imprint","INTERSECT",VERTEX,{"derivedFrom":[sQuery(id+"F0.wireOp",EDGE,"E4"),subQ1,sQuery(id+"F0.wireOp",EDGE,"E9"),sQuery(id+"F0.wireOp",EDGE,"E26"),sQuery(id+"F0.wireOp",EDGE,"E32"),subQ0]});Q71=makeQuery(id+"F0.imprint","IMPRINT",FACE,{"disambiguationData":[TD([[makeQuery(id+"F0.imprint","IMPRINT",EDGE,{"disambiguationData":[TD([[subQ2,1.0]])],"derivedFrom":subQ1}),1.0]])]});}
            var Q72;
            {var subQ0=sQuery(id+"F0.wireOp",EDGE,"E31");var subQ1=sQuery(id+"F0.wireOp",EDGE,"E17");var subQ2=makeQuery(id+"F0.imprint","INTERSECT",VERTEX,{"derivedFrom":[sQuery(id+"F0.wireOp",EDGE,"E4"),sQuery(id+"F0.wireOp",EDGE,"E5"),sQuery(id+"F0.wireOp",EDGE,"E10"),subQ1,subQ0,sQuery(id+"F0.wireOp",EDGE,"E32")]});Q72=makeQuery(id+"F0.imprint","IMPRINT",FACE,{"disambiguationData":[TD([[makeQuery(id+"F0.imprint","IMPRINT",EDGE,{"disambiguationData":[TD([[subQ2,-1.0]])],"derivedFrom":subQ1}),1.0]])]});}
            var Q73;
            {var subQ0=sQuery(id+"F0.wireOp",EDGE,"E45");var subQ1=sQuery(id+"F0.wireOp",EDGE,"E8");var subQ2=makeQuery(id+"F0.imprint","INTERSECT",VERTEX,{"derivedFrom":[subQ1,sQuery(id+"F0.wireOp",EDGE,"E10"),sQuery(id+"F0.wireOp",EDGE,"E32"),sQuery(id+"F0.wireOp",EDGE,"E38"),subQ0,sQuery(id+"F0.wireOp",EDGE,"E46")]});Q73=makeQuery(id+"F0.imprint","IMPRINT",FACE,{"disambiguationData":[TD([[makeQuery(id+"F0.imprint","IMPRINT",EDGE,{"disambiguationData":[TD([[subQ2,-1.0]])],"derivedFrom":subQ1}),1.0]])]});}
            var Q74;
            {var subQ0=sQuery(id+"F0.wireOp",EDGE,"E32");var subQ1=sQuery(id+"F0.wireOp",EDGE,"E10");var subQ2=makeQuery(id+"F0.imprint","INTERSECT",VERTEX,{"derivedFrom":[sQuery(id+"F0.wireOp",EDGE,"E4"),sQuery(id+"F0.wireOp",EDGE,"E5"),subQ1,sQuery(id+"F0.wireOp",EDGE,"E17"),sQuery(id+"F0.wireOp",EDGE,"E31"),subQ0]});Q74=makeQuery(id+"F0.imprint","IMPRINT",FACE,{"disambiguationData":[TD([[makeQuery(id+"F0.imprint","IMPRINT",EDGE,{"disambiguationData":[TD([[subQ2,1.0]])],"derivedFrom":subQ1}),1.0]])]});}
            var Q75;
            {var subQ0=sQuery(id+"F0.wireOp",EDGE,"E38");var subQ1=sQuery(id+"F0.wireOp",EDGE,"E8");var subQ2=makeQuery(id+"F0.imprint","INTERSECT",VERTEX,{"derivedFrom":[sQuery(id+"F0.wireOp",EDGE,"E5"),subQ1,sQuery(id+"F0.wireOp",EDGE,"E11"),sQuery(id+"F0.wireOp",EDGE,"E14"),sQuery(id+"F0.wireOp",EDGE,"E31"),subQ0]});Q75=makeQuery(id+"F0.imprint","IMPRINT",FACE,{"disambiguationData":[TD([[makeQuery(id+"F0.imprint","IMPRINT",EDGE,{"disambiguationData":[TD([[subQ2,-1.0]])],"derivedFrom":subQ1}),1.0]])]});}
            var Q76;
            {var subQ0=sQuery(id+"F0.wireOp",EDGE,"E46");var subQ1=sQuery(id+"F0.wireOp",EDGE,"E10");var subQ2=makeQuery(id+"F0.imprint","INTERSECT",VERTEX,{"derivedFrom":[subQ1,sQuery(id+"F0.wireOp",EDGE,"E14"),sQuery(id+"F0.wireOp",EDGE,"E31"),subQ0,sQuery(id+"F0.wireOp",EDGE,"E48")]});Q76=makeQuery(id+"F0.imprint","IMPRINT",FACE,{"disambiguationData":[TD([[makeQuery(id+"F0.imprint","IMPRINT",EDGE,{"disambiguationData":[TD([[subQ2,-1.0]])],"derivedFrom":subQ1}),1.0]])]});}
            var Q77;
            {var subQ0=sQuery(id+"F0.wireOp",EDGE,"E31");var subQ1=sQuery(id+"F0.wireOp",EDGE,"E14");var subQ2=makeQuery(id+"F0.imprint","INTERSECT",VERTEX,{"derivedFrom":[sQuery(id+"F0.wireOp",EDGE,"E10"),subQ1,subQ0,sQuery(id+"F0.wireOp",EDGE,"E46"),sQuery(id+"F0.wireOp",EDGE,"E48")]});Q77=makeQuery(id+"F0.imprint","IMPRINT",FACE,{"disambiguationData":[TD([[makeQuery(id+"F0.imprint","IMPRINT",EDGE,{"disambiguationData":[TD([[subQ2,-1.0]])],"derivedFrom":subQ1}),1.0]])]});}
            var Q78;
            {var subQ0=sQuery(id+"F0.wireOp",EDGE,"E48");var subQ1=sQuery(id+"F0.wireOp",EDGE,"E10");var subQ2=makeQuery(id+"F0.imprint","INTERSECT",VERTEX,{"derivedFrom":[subQ1,sQuery(id+"F0.wireOp",EDGE,"E14"),sQuery(id+"F0.wireOp",EDGE,"E31"),sQuery(id+"F0.wireOp",EDGE,"E46"),subQ0]});Q78=makeQuery(id+"F0.imprint","IMPRINT",FACE,{"disambiguationData":[TD([[makeQuery(id+"F0.imprint","IMPRINT",EDGE,{"disambiguationData":[TD([[subQ2,1.0]])],"derivedFrom":subQ1}),1.0]])]});}
            var Q79;
            {var subQ0=sQuery(id+"F0.wireOp",EDGE,"E50");var subQ1=sQuery(id+"F0.wireOp",EDGE,"E12");var subQ2=makeQuery(id+"F0.imprint","INTERSECT",VERTEX,{"derivedFrom":[subQ1,sQuery(id+"F0.wireOp",EDGE,"E13"),sQuery(id+"F0.wireOp",EDGE,"E29"),subQ0]});Q79=makeQuery(id+"F0.imprint","IMPRINT",FACE,{"disambiguationData":[TD([[makeQuery(id+"F0.imprint","IMPRINT",EDGE,{"disambiguationData":[TD([[subQ2,-1.0]])],"derivedFrom":subQ1}),1.0]])]});}
            var Q80;
            {var subQ0=sQuery(id+"F0.wireOp",EDGE,"E29");var subQ1=sQuery(id+"F0.wireOp",EDGE,"E13");var subQ2=makeQuery(id+"F0.imprint","INTERSECT",VERTEX,{"derivedFrom":[sQuery(id+"F0.wireOp",EDGE,"E12"),subQ1,subQ0,sQuery(id+"F0.wireOp",EDGE,"E50")]});Q80=makeQuery(id+"F0.imprint","IMPRINT",FACE,{"disambiguationData":[TD([[makeQuery(id+"F0.imprint","IMPRINT",EDGE,{"disambiguationData":[TD([[subQ2,1.0]])],"derivedFrom":subQ1}),1.0]])]});}
            var Q81;
            {var subQ0=sQuery(id+"F0.wireOp",EDGE,"E37");var subQ1=sQuery(id+"F0.wireOp",EDGE,"E7");var subQ2=makeQuery(id+"F0.imprint","INTERSECT",VERTEX,{"derivedFrom":[subQ1,sQuery(id+"F0.wireOp",EDGE,"E12"),sQuery(id+"F0.wireOp",EDGE,"E30"),subQ0]});Q81=makeQuery(id+"F0.imprint","IMPRINT",FACE,{"disambiguationData":[TD([[makeQuery(id+"F0.imprint","IMPRINT",EDGE,{"disambiguationData":[TD([[subQ2,-1.0]])],"derivedFrom":subQ1}),1.0]])]});}
            var Q82;
            {var subQ0=sQuery(id+"F0.wireOp",EDGE,"E30");var subQ1=sQuery(id+"F0.wireOp",EDGE,"E12");var subQ2=makeQuery(id+"F0.imprint","INTERSECT",VERTEX,{"derivedFrom":[sQuery(id+"F0.wireOp",EDGE,"E7"),subQ1,subQ0,sQuery(id+"F0.wireOp",EDGE,"E37")]});Q82=makeQuery(id+"F0.imprint","IMPRINT",FACE,{"disambiguationData":[TD([[makeQuery(id+"F0.imprint","IMPRINT",EDGE,{"disambiguationData":[TD([[subQ2,1.0]])],"derivedFrom":subQ1}),1.0]])]});}
            var Q83;
            {var subQ0=sQuery(id+"F0.wireOp",EDGE,"E29");var subQ1=sQuery(id+"F0.wireOp",EDGE,"E16");var subQ2=makeQuery(id+"F0.imprint","INTERSECT",VERTEX,{"derivedFrom":[sQuery(id+"F0.wireOp",EDGE,"E7"),subQ1,subQ0,sQuery(id+"F0.wireOp",EDGE,"E33")]});Q83=makeQuery(id+"F0.imprint","IMPRINT",FACE,{"disambiguationData":[TD([[makeQuery(id+"F0.imprint","IMPRINT",EDGE,{"disambiguationData":[TD([[subQ2,-1.0]])],"derivedFrom":subQ1}),1.0]])]});}
            var Q84;
            {var subQ0=sQuery(id+"F0.wireOp",EDGE,"E33");var subQ1=sQuery(id+"F0.wireOp",EDGE,"E7");var subQ2=makeQuery(id+"F0.imprint","INTERSECT",VERTEX,{"derivedFrom":[subQ1,sQuery(id+"F0.wireOp",EDGE,"E16"),sQuery(id+"F0.wireOp",EDGE,"E29"),subQ0]});Q84=makeQuery(id+"F0.imprint","IMPRINT",FACE,{"disambiguationData":[TD([[makeQuery(id+"F0.imprint","IMPRINT",EDGE,{"disambiguationData":[TD([[subQ2,1.0]])],"derivedFrom":subQ1}),1.0]])]});}
            var Q85;
            {var subQ0=sQuery(id+"F0.wireOp",EDGE,"E30");var subQ1=sQuery(id+"F0.wireOp",EDGE,"E24");var subQ2=makeQuery(id+"F0.imprint","INTERSECT",VERTEX,{"derivedFrom":[sQuery(id+"F0.wireOp",EDGE,"E16"),subQ1,subQ0,sQuery(id+"F0.wireOp",EDGE,"E51")]});Q85=makeQuery(id+"F0.imprint","IMPRINT",FACE,{"disambiguationData":[TD([[makeQuery(id+"F0.imprint","IMPRINT",EDGE,{"disambiguationData":[TD([[subQ2,-1.0]])],"derivedFrom":subQ1}),1.0]])]});}
            var Q86;
            {var subQ0=sQuery(id+"F0.wireOp",EDGE,"E51");var subQ1=sQuery(id+"F0.wireOp",EDGE,"E16");var subQ2=makeQuery(id+"F0.imprint","INTERSECT",VERTEX,{"derivedFrom":[subQ1,sQuery(id+"F0.wireOp",EDGE,"E24"),sQuery(id+"F0.wireOp",EDGE,"E30"),subQ0]});Q86=makeQuery(id+"F0.imprint","IMPRINT",FACE,{"disambiguationData":[TD([[makeQuery(id+"F0.imprint","IMPRINT",EDGE,{"disambiguationData":[TD([[subQ2,1.0]])],"derivedFrom":subQ1}),1.0]])]});}
            var Q87;
            {var subQ0=sQuery(id+"F0.wireOp",EDGE,"E52");var subQ1=sQuery(id+"F0.wireOp",EDGE,"E12");var subQ2=makeQuery(id+"F0.imprint","INTERSECT",VERTEX,{"derivedFrom":[sQuery(id+"F0.wireOp",EDGE,"E7"),subQ1,sQuery(id+"F0.wireOp",EDGE,"E30"),sQuery(id+"F0.wireOp",EDGE,"E37"),subQ0,sQuery(id+"F0.wireOp",EDGE,"E53")]});Q87=makeQuery(id+"F0.imprint","IMPRINT",FACE,{"disambiguationData":[TD([[makeQuery(id+"F0.imprint","IMPRINT",EDGE,{"disambiguationData":[TD([[subQ2,-1.0]])],"derivedFrom":subQ1}),1.0]])]});}
            var Q88;
            {var subQ0=sQuery(id+"F0.wireOp",EDGE,"E53");var subQ1=sQuery(id+"F0.wireOp",EDGE,"E7");var subQ2=makeQuery(id+"F0.imprint","INTERSECT",VERTEX,{"derivedFrom":[subQ1,sQuery(id+"F0.wireOp",EDGE,"E12"),sQuery(id+"F0.wireOp",EDGE,"E30"),sQuery(id+"F0.wireOp",EDGE,"E37"),sQuery(id+"F0.wireOp",EDGE,"E52"),subQ0]});Q88=makeQuery(id+"F0.imprint","IMPRINT",FACE,{"disambiguationData":[TD([[makeQuery(id+"F0.imprint","IMPRINT",EDGE,{"disambiguationData":[TD([[subQ2,1.0]])],"derivedFrom":subQ1}),1.0]])]});}
            var Q89;
            {var subQ0=sQuery(id+"F0.wireOp",EDGE,"E54");var subQ1=sQuery(id+"F0.wireOp",EDGE,"E16");var subQ2=makeQuery(id+"F0.imprint","INTERSECT",VERTEX,{"derivedFrom":[sQuery(id+"F0.wireOp",EDGE,"E7"),subQ1,sQuery(id+"F0.wireOp",EDGE,"E29"),sQuery(id+"F0.wireOp",EDGE,"E33"),sQuery(id+"F0.wireOp",EDGE,"E53"),subQ0]});Q89=makeQuery(id+"F0.imprint","IMPRINT",FACE,{"disambiguationData":[TD([[makeQuery(id+"F0.imprint","IMPRINT",EDGE,{"disambiguationData":[TD([[subQ2,1.0]])],"derivedFrom":subQ1}),1.0]])]});}
            extrude(context, id + "F1", {"entities" : qUnion([Q0, Q1, Q2, Q3, Q4, Q5, Q6, Q7, Q8, Q9, Q10, Q11, Q12, Q13, Q14, Q15, Q16, Q17, Q18, Q19, Q20, Q21, Q22, Q23, Q24, Q25, Q26, Q27, Q28, Q29, Q30, Q31, Q32, Q33, Q34, Q35, Q36, Q37, Q38, Q39, Q40, Q41, Q42, Q43, Q44, Q45, Q46, Q47, Q48, Q49, Q50, Q51, Q52, Q53, Q54, Q55, Q56, Q57, Q58, Q59, Q60, Q61, Q62, Q63, Q64, Q65, Q66, Q67, Q68, Q69, Q70, Q71, Q72, Q73, Q74, Q75, Q76, Q77, Q78, Q79, Q80, Q81, Q82, Q83, Q84, Q85, Q86, Q87, Q88, Q89]), "depth" : 4 * mm, "offsetDistance" : 25 * mm});
        }
        {
            var Q0;
            Q0=qCreatedBy(makeId("Top.planeOp"),FACE);
            var sketch = newSketch(context, id + "F2", { "sketchPlane" : qUnion([Q0])});
            skCircle(sketch, "E55", {"center": v(0, 0) * mm, "radius": 45 * mm});
            skSolve(sketch);
        }
        {
            var Q0;
            Q0=makeQuery(id+"F2.imprint","IMPRINT",FACE,{"disambiguationData":[TD([[makeQuery(id+"F2.imprint","IMPRINT",EDGE,{"derivedFrom":sQuery(id+"F2.wireOp",EDGE,"E55")}),1.0]])]});
            extrude(context, id + "F3", {"entities" : qUnion([Q0]), "depth" : -2 * mm, "offsetDistance" : 25 * mm});
        }
        {
            var Q0;
            Q0=makeQuery(id+"F3.opExtrude","CAP_FACE",FACE,{"disambiguationData":[OSD([sQuery(id+"F2.wireOp",EDGE,"E55")])],"isStart":false});
            var sketch = newSketch(context, id + "F4", { "sketchPlane" : qUnion([Q0])});
            skCircle(sketch, "E56", {"center": v(0, 38) * mm, "radius": 2 * mm});
            skLineSegment(sketch, "E57", {"start": v(0, 45) * mm, "end": v(0, 40) * mm});
            skLineSegment(sketch, "E58", {"start": v(0, 36) * mm, "end": v(0, 31) * mm});
            skLineSegment(sketch, "E59", {"start": v(-6.71, 31) * mm, "end": v(8.6, 31) * mm});
            skSolve(sketch);
        }
        {
            var Q0;
            Q0=makeQuery(id+"F4.imprint","IMPRINT",FACE,{"disambiguationData":[TD([[makeQuery(id+"F4.imprint","IMPRINT",EDGE,{"derivedFrom":makeQuery(id+"F3.opExtrude","CAP_EDGE",EDGE,{"disambiguationData":[OSD([sQuery(id+"F2.wireOp",EDGE,"E55")])],"isStart":false})}),-1.0]])]});
            var sketch = newSketch(context, id + "F5", { "sketchPlane" : qUnion([Q0])});
            skCircle(sketch, "E60", {"center": v(0, 0) * mm, "radius": 9.54 * mm});
            skSolve(sketch);
        }
        {
            var Q0;
            Q0=makeQuery(id+"F4.imprint","IMPRINT",FACE,{"disambiguationData":[TD([[makeQuery(id+"F4.imprint","IMPRINT",EDGE,{"derivedFrom":makeQuery(id+"F3.opExtrude","CAP_EDGE",EDGE,{"disambiguationData":[OSD([sQuery(id+"F2.wireOp",EDGE,"E55")])],"isStart":false})}),-1.0]])]});
            extrude(context, id + "F6", {"entities" : qUnion([Q0]), "operationType" : NewBodyOperationType.ADD, "depth" : 25 * mm, "offsetDistance" : 25 * mm});
        }
    });
